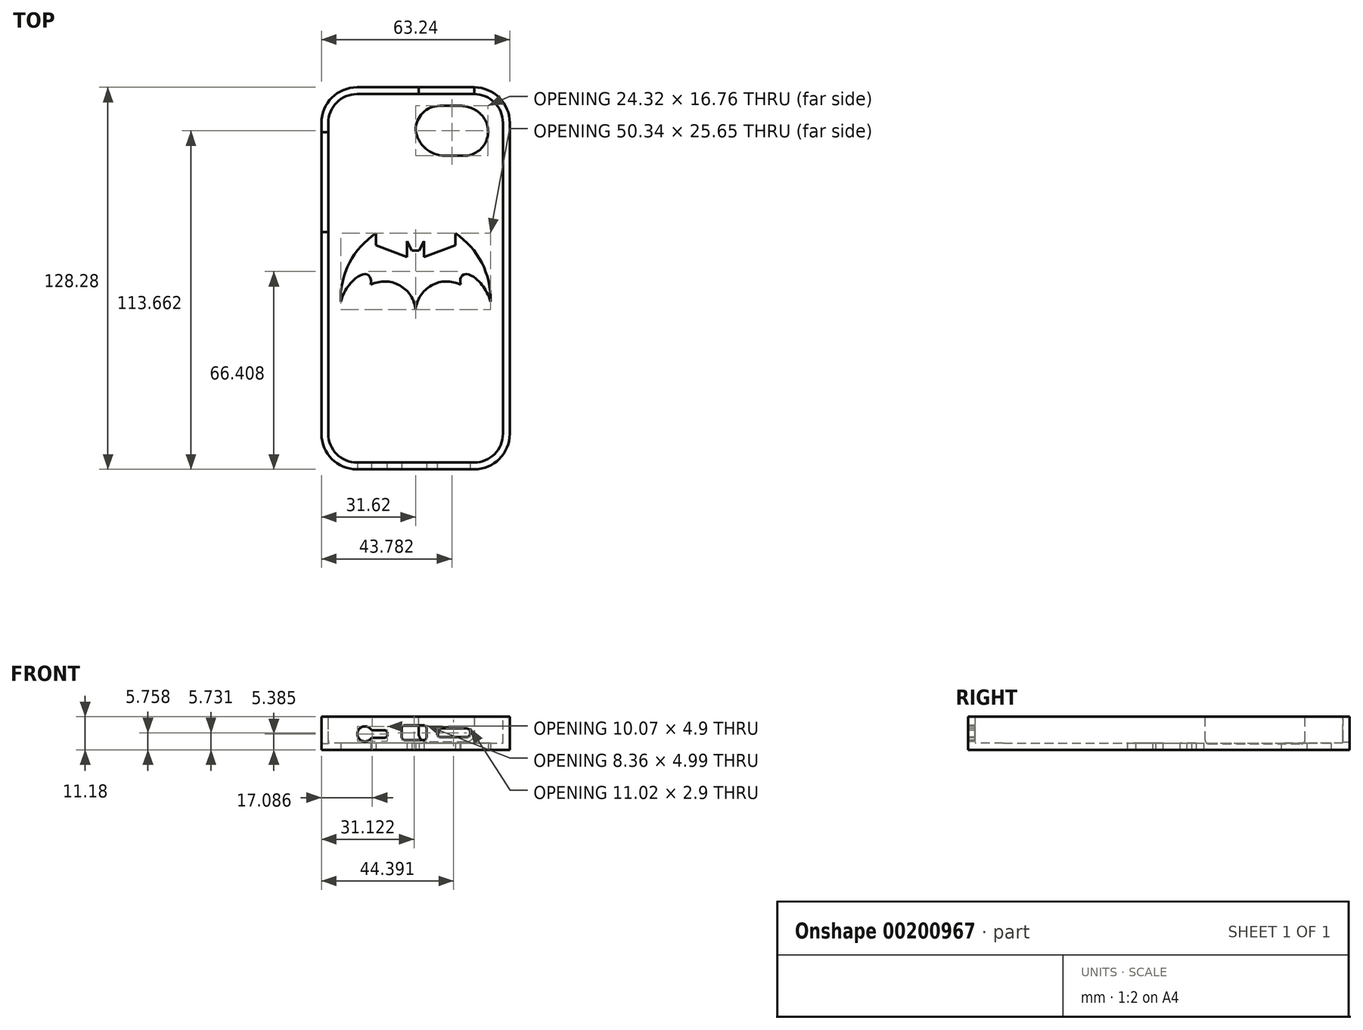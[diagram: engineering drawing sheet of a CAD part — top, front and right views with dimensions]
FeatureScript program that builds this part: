
annotation { "Feature Type Name" : "Feature", "Feature Type Description" : "" }
export const myFeature = defineFeature(function(context is Context, id is Id, definition is map)
    precondition{}
    {
        {
            var Q0;
            Q0=qCreatedBy(makeId("Top.planeOp"),FACE);
            var sketch = newSketch(context, id + "F0", { "sketchPlane" : qUnion([Q0])});
            skLineSegment(sketch, "E0.bottom", {"start": v(31.62, -64.13) * mm, "end": v(-31.62, -64.13) * mm});
            skLineSegment(sketch, "E0.top", {"start": v(31.62, 64.13) * mm, "end": v(-31.62, 64.13) * mm});
            skLineSegment(sketch, "E0.left", {"start": v(31.62, -64.13) * mm, "end": v(31.62, 64.14) * mm});
            skLineSegment(sketch, "E0.right", {"start": v(-31.62, -64.13) * mm, "end": v(-31.62, 64.14) * mm});
            skPoint(sketch, "E0.middle", {"position": v(0, 0) * mm});
            skSolve(sketch);
        }
        {
            var Q0;
            Q0=makeQuery(id+"F0.imprint","IMPRINT",FACE,{"disambiguationData":[TD([[makeQuery(id+"F0.imprint","IMPRINT",EDGE,{"derivedFrom":sQuery(id+"F0.wireOp",EDGE,"E0.bottom")}),-1.0]])]});
            extrude(context, id + "F1", {"entities" : qUnion([Q0]), "depth" : 11.18 * mm});
        }
        {
            var Q0;
            Q0=makeQuery(id+"F1.opExtrude","SWEPT_EDGE",EDGE,{"disambiguationData":[OSD([sQuery(id+"F0.wireOp",EDGE,"E0.bottom"),sQuery(id+"F0.wireOp",EDGE,"E0.right")])]});
            fillet(context, id + "F2", {"entities" : qUnion([Q0]), "radius" : 11.94 * mm, "tangentPropagation" : true, "allowEdgeOverflow" : false});
        }
        {
            var Q0;
            Q0=makeQuery(id+"F1.opExtrude","SWEPT_EDGE",EDGE,{"disambiguationData":[OSD([sQuery(id+"F0.wireOp",EDGE,"E0.bottom"),sQuery(id+"F0.wireOp",EDGE,"E0.left")])]});
            fillet(context, id + "F3", {"entities" : qUnion([Q0]), "radius" : 11.94 * mm, "tangentPropagation" : true, "allowEdgeOverflow" : false});
        }
        {
            var Q0;
            Q0=makeQuery(id+"F1.opExtrude","SWEPT_EDGE",EDGE,{"disambiguationData":[OSD([sQuery(id+"F0.wireOp",EDGE,"E0.top"),sQuery(id+"F0.wireOp",EDGE,"E0.right")])]});
            fillet(context, id + "F4", {"entities" : qUnion([Q0]), "radius" : 11.94 * mm, "tangentPropagation" : true, "allowEdgeOverflow" : false});
        }
        {
            var Q0;
            Q0=makeQuery(id+"F1.opExtrude","SWEPT_EDGE",EDGE,{"disambiguationData":[OSD([sQuery(id+"F0.wireOp",EDGE,"E0.top"),sQuery(id+"F0.wireOp",EDGE,"E0.left")])]});
            fillet(context, id + "F5", {"entities" : qUnion([Q0]), "radius" : 11.94 * mm, "tangentPropagation" : true, "allowEdgeOverflow" : false});
        }
        {
            var Q0;
            Q0=makeQuery(id+"F1.opExtrude","CAP_FACE",FACE,{"disambiguationData":[OSD([sQuery(id+"F0.wireOp",EDGE,"E0.bottom"),sQuery(id+"F0.wireOp",EDGE,"E0.top"),sQuery(id+"F0.wireOp",EDGE,"E0.left"),sQuery(id+"F0.wireOp",EDGE,"E0.right")])],"isStart":false});
            shell(context, id + "F6", {"entities" : qUnion([Q0]), "thickness" : 2.3 * mm});
        }
        {
            var Q0;
            Q0=makeQuery(id+"F1.opExtrude","CAP_FACE",FACE,{"disambiguationData":[OSD([sQuery(id+"F0.wireOp",EDGE,"E0.bottom"),sQuery(id+"F0.wireOp",EDGE,"E0.top"),sQuery(id+"F0.wireOp",EDGE,"E0.left"),sQuery(id+"F0.wireOp",EDGE,"E0.right")])],"isStart":true});
            var sketch = newSketch(context, id + "F7", { "sketchPlane" : qUnion([Q0])});
            skLineSegment(sketch, "E1", {"start": v(24.9, -57.9) * mm, "end": v(0, -57.9) * mm});
            skLineSegment(sketch, "E2", {"start": v(0, -57.9) * mm, "end": v(0, -41.14) * mm});
            skLineSegment(sketch, "E3", {"start": v(24.9, -57.9) * mm, "end": v(24.9, -41.14) * mm});
            skLineSegment(sketch, "E4", {"start": v(24.9, -41.14) * mm, "end": v(0, -41.14) * mm});
            skSolve(sketch);
        }
        {
            var Q0;
            Q0=makeQuery(id+"F7.imprint","IMPRINT",FACE,{"disambiguationData":[TD([[makeQuery(id+"F7.imprint","IMPRINT",EDGE,{"derivedFrom":sQuery(id+"F7.wireOp",EDGE,"E1")}),-1.0]])]});
            extrude(context, id + "F8", {"entities" : qUnion([Q0]), "operationType" : NewBodyOperationType.REMOVE, "oppositeDirection" : true, "depth" : 25.4 * mm});
        }
        {
            var Q0;
            Q0=makeQuery(id+"F8.boolean.opBoolean","COPY",EDGE,{"derivedFrom":makeQuery(id+"F8.opExtrude","SWEPT_EDGE",EDGE,{"disambiguationData":[OSD([sQuery(id+"F7.wireOp",EDGE,"E1"),sQuery(id+"F7.wireOp",EDGE,"E2")])]})});
            fillet(context, id + "F9", {"entities" : qUnion([Q0]), "radius" : 8.13 * mm, "tangentPropagation" : true, "allowEdgeOverflow" : false});
        }
        {
            var Q0;
            Q0=makeQuery(id+"F8.boolean.opBoolean","COPY",EDGE,{"derivedFrom":makeQuery(id+"F8.opExtrude","SWEPT_EDGE",EDGE,{"disambiguationData":[OSD([sQuery(id+"F7.wireOp",EDGE,"E1"),sQuery(id+"F7.wireOp",EDGE,"E3")])]})});
            fillet(context, id + "F10", {"entities" : qUnion([Q0]), "radius" : 9.9 * mm, "tangentPropagation" : true, "allowEdgeOverflow" : false});
        }
        {
            var Q0;
            Q0=makeQuery(id+"F8.boolean.opBoolean","COPY",EDGE,{"derivedFrom":makeQuery(id+"F8.opExtrude","SWEPT_EDGE",EDGE,{"disambiguationData":[OSD([sQuery(id+"F7.wireOp",EDGE,"E3"),sQuery(id+"F7.wireOp",EDGE,"E4")])]})});
            fillet(context, id + "F11", {"entities" : qUnion([Q0]), "radius" : 8.13 * mm, "tangentPropagation" : true, "allowEdgeOverflow" : false});
        }
        {
            var Q0;
            Q0=makeQuery(id+"F8.boolean.opBoolean","COPY",EDGE,{"derivedFrom":makeQuery(id+"F8.opExtrude","SWEPT_EDGE",EDGE,{"disambiguationData":[OSD([sQuery(id+"F7.wireOp",EDGE,"E2"),sQuery(id+"F7.wireOp",EDGE,"E4")])]})});
            fillet(context, id + "F12", {"entities" : qUnion([Q0]), "radius" : 9.9 * mm, "tangentPropagation" : true, "allowEdgeOverflow" : false});
        }
        {
            var Q0;
            Q0=makeQuery(id+"F1.opExtrude","CAP_FACE",FACE,{"disambiguationData":[OSD([sQuery(id+"F0.wireOp",EDGE,"E0.bottom"),sQuery(id+"F0.wireOp",EDGE,"E0.top"),sQuery(id+"F0.wireOp",EDGE,"E0.left"),sQuery(id+"F0.wireOp",EDGE,"E0.right")])],"isStart":false});
            var sketch = newSketch(context, id + "F13", { "sketchPlane" : qUnion([Q0])});
            skLineSegment(sketch, "E5.bottom", {"start": v(-29.34, 49.08) * mm, "end": v(-31.62, 49.08) * mm});
            skLineSegment(sketch, "E5.top", {"start": v(-29.34, 15.55) * mm, "end": v(-31.62, 15.55) * mm});
            skLineSegment(sketch, "E5.left", {"start": v(-29.34, 49.08) * mm, "end": v(-29.34, 15.55) * mm});
            skLineSegment(sketch, "E5.right", {"start": v(-31.62, 49.08) * mm, "end": v(-31.62, 15.55) * mm});
            skSolve(sketch);
        }
        {
            var Q0;
            Q0=makeQuery(id+"F13.imprint","IMPRINT",FACE,{"disambiguationData":[TD([[makeQuery(id+"F13.imprint","IMPRINT",EDGE,{"derivedFrom":sQuery(id+"F13.wireOp",EDGE,"E5.bottom")}),1.0]])]});
            extrude(context, id + "F14", {"entities" : qUnion([Q0]), "operationType" : NewBodyOperationType.REMOVE, "oppositeDirection" : true, "depth" : 9.14 * mm});
        }
        {
            var Q0;
            Q0=makeQuery(id+"F14.boolean.opBoolean","COPY",EDGE,{"derivedFrom":makeQuery(id+"F14.opExtrude","CAP_EDGE",EDGE,{"disambiguationData":[OSD([sQuery(id+"F13.wireOp",EDGE,"E5.bottom")])],"isStart":false})});
            fillet(context, id + "F15", {"entities" : qUnion([Q0]), "radius" : 1.23 * mm, "tangentPropagation" : true, "allowEdgeOverflow" : false});
        }
        {
            var Q0;
            Q0=makeQuery(id+"F14.boolean.opBoolean","COPY",EDGE,{"derivedFrom":makeQuery(id+"F14.opExtrude","CAP_EDGE",EDGE,{"disambiguationData":[OSD([sQuery(id+"F13.wireOp",EDGE,"E5.top")])],"isStart":false})});
            fillet(context, id + "F16", {"entities" : qUnion([Q0]), "radius" : 1.22 * mm, "tangentPropagation" : true, "allowEdgeOverflow" : false});
        }
        {
            var Q0;
            Q0=makeQuery(id+"F1.opExtrude","SWEPT_FACE",FACE,{"disambiguationData":[OSD([sQuery(id+"F0.wireOp",EDGE,"E0.bottom")])]});
            var sketch = newSketch(context, id + "F17", { "sketchPlane" : qUnion([Q0])});
            skArc(sketch, "E6", {"start": v(-14.81, 6.6) * mm, "mid": v(-19.57, 5.42) * mm, "end": v(-14.87, 4.04) * mm});
            skLineSegment(sketch, "E7", {"start": v(-14.81, 6.6) * mm, "end": v(-9.48, 6.6) * mm});
            skLineSegment(sketch, "E8", {"start": v(-14.87, 4.04) * mm, "end": v(-9.53, 4.04) * mm});
            skLineSegment(sketch, "E9", {"start": v(-9.48, 6.6) * mm, "end": v(-9.53, 4.04) * mm});
            skSolve(sketch);
        }
        {
            var Q0;
            Q0=makeQuery(id+"F17.imprint","IMPRINT",FACE,{"disambiguationData":[TD([[makeQuery(id+"F17.imprint","IMPRINT",EDGE,{"derivedFrom":sQuery(id+"F17.wireOp",EDGE,"E6")}),1.0]])]});
            extrude(context, id + "F18", {"entities" : qUnion([Q0]), "operationType" : NewBodyOperationType.REMOVE, "oppositeDirection" : true, "depth" : 25.4 * mm});
        }
        {
            var Q0;
            Q0=makeQuery(id+"F18.boolean.opBoolean","COPY",EDGE,{"derivedFrom":makeQuery(id+"F18.opExtrude","SWEPT_EDGE",EDGE,{"disambiguationData":[OSD([sQuery(id+"F17.wireOp",EDGE,"E7"),sQuery(id+"F17.wireOp",EDGE,"E9")])]})});
            fillet(context, id + "F19", {"entities" : qUnion([Q0]), "radius" : 1.02 * mm, "tangentPropagation" : true, "allowEdgeOverflow" : false});
        }
        {
            var Q0;
            Q0=makeQuery(id+"F18.boolean.opBoolean","COPY",EDGE,{"derivedFrom":makeQuery(id+"F18.opExtrude","SWEPT_EDGE",EDGE,{"disambiguationData":[OSD([sQuery(id+"F17.wireOp",EDGE,"E8"),sQuery(id+"F17.wireOp",EDGE,"E9")])]})});
            fillet(context, id + "F20", {"entities" : qUnion([Q0]), "radius" : 1.02 * mm, "tangentPropagation" : true, "allowEdgeOverflow" : false});
        }
        {
            var Q0;
            Q0=makeQuery(id+"F1.opExtrude","SWEPT_FACE",FACE,{"disambiguationData":[OSD([sQuery(id+"F0.wireOp",EDGE,"E0.bottom")])]});
            var sketch = newSketch(context, id + "F21", { "sketchPlane" : qUnion([Q0])});
            skLineSegment(sketch, "E10.bottom", {"start": v(3.68, 3.27) * mm, "end": v(-4.68, 3.27) * mm});
            skLineSegment(sketch, "E10.top", {"start": v(3.68, 8.25) * mm, "end": v(-4.68, 8.25) * mm});
            skLineSegment(sketch, "E10.left", {"start": v(3.68, 3.27) * mm, "end": v(3.68, 8.25) * mm});
            skLineSegment(sketch, "E10.right", {"start": v(-4.68, 3.27) * mm, "end": v(-4.68, 8.25) * mm});
            skSolve(sketch);
        }
        {
            var Q0;
            Q0=makeQuery(id+"F21.imprint","IMPRINT",FACE,{"disambiguationData":[TD([[makeQuery(id+"F21.imprint","IMPRINT",EDGE,{"derivedFrom":sQuery(id+"F21.wireOp",EDGE,"E10.bottom")}),-1.0]])]});
            extrude(context, id + "F22", {"entities" : qUnion([Q0]), "operationType" : NewBodyOperationType.REMOVE, "oppositeDirection" : true, "depth" : 25.4 * mm});
        }
        {
            var Q0;
            Q0=makeQuery(id+"F22.boolean.opBoolean","COPY",EDGE,{"derivedFrom":makeQuery(id+"F22.opExtrude","SWEPT_EDGE",EDGE,{"disambiguationData":[OSD([sQuery(id+"F21.wireOp",EDGE,"E10.bottom"),sQuery(id+"F21.wireOp",EDGE,"E10.right")])]})});
            fillet(context, id + "F23", {"entities" : qUnion([Q0]), "radius" : 1.1 * mm, "tangentPropagation" : true, "allowEdgeOverflow" : false});
        }
        {
            var Q0;
            Q0=makeQuery(id+"F22.boolean.opBoolean","COPY",EDGE,{"derivedFrom":makeQuery(id+"F22.opExtrude","SWEPT_EDGE",EDGE,{"disambiguationData":[OSD([sQuery(id+"F21.wireOp",EDGE,"E10.bottom"),sQuery(id+"F21.wireOp",EDGE,"E10.left")])]})});
            fillet(context, id + "F24", {"entities" : qUnion([Q0]), "radius" : 1.1 * mm, "tangentPropagation" : true, "allowEdgeOverflow" : false});
        }
        {
            var Q0;
            Q0=makeQuery(id+"F22.boolean.opBoolean","COPY",EDGE,{"derivedFrom":makeQuery(id+"F22.opExtrude","SWEPT_EDGE",EDGE,{"disambiguationData":[OSD([sQuery(id+"F21.wireOp",EDGE,"E10.top"),sQuery(id+"F21.wireOp",EDGE,"E10.right")])]})});
            fillet(context, id + "F25", {"entities" : qUnion([Q0]), "radius" : 1.1 * mm, "tangentPropagation" : true, "allowEdgeOverflow" : false});
        }
        {
            var Q0;
            Q0=makeQuery(id+"F22.boolean.opBoolean","COPY",EDGE,{"derivedFrom":makeQuery(id+"F22.opExtrude","SWEPT_EDGE",EDGE,{"disambiguationData":[OSD([sQuery(id+"F21.wireOp",EDGE,"E10.top"),sQuery(id+"F21.wireOp",EDGE,"E10.left")])]})});
            fillet(context, id + "F26", {"entities" : qUnion([Q0]), "radius" : 1.1 * mm, "tangentPropagation" : true, "allowEdgeOverflow" : false});
        }
        {
            var Q0;
            Q0=makeQuery(id+"F1.opExtrude","SWEPT_FACE",FACE,{"disambiguationData":[OSD([sQuery(id+"F0.wireOp",EDGE,"E0.bottom")])]});
            var sketch = newSketch(context, id + "F27", { "sketchPlane" : qUnion([Q0])});
            skLineSegment(sketch, "E11.bottom", {"start": v(7.26, 7.18) * mm, "end": v(18.28, 7.18) * mm});
            skLineSegment(sketch, "E11.top", {"start": v(7.26, 4.28) * mm, "end": v(18.28, 4.28) * mm});
            skLineSegment(sketch, "E11.left", {"start": v(7.26, 7.18) * mm, "end": v(7.26, 4.28) * mm});
            skLineSegment(sketch, "E11.right", {"start": v(18.28, 7.18) * mm, "end": v(18.28, 4.28) * mm});
            skSolve(sketch);
        }
        {
            var Q0;
            Q0=makeQuery(id+"F27.imprint","IMPRINT",FACE,{"disambiguationData":[TD([[makeQuery(id+"F27.imprint","IMPRINT",EDGE,{"derivedFrom":sQuery(id+"F27.wireOp",EDGE,"E11.bottom")}),-1.0]])]});
            extrude(context, id + "F28", {"entities" : qUnion([Q0]), "operationType" : NewBodyOperationType.REMOVE, "oppositeDirection" : true, "depth" : 23.72 * mm});
        }
        {
            var Q0;
            Q0=makeQuery(id+"F28.boolean.opBoolean","COPY",EDGE,{"derivedFrom":makeQuery(id+"F28.opExtrude","SWEPT_EDGE",EDGE,{"disambiguationData":[OSD([sQuery(id+"F27.wireOp",EDGE,"E11.bottom"),sQuery(id+"F27.wireOp",EDGE,"E11.left")])]})});
            fillet(context, id + "F29", {"entities" : qUnion([Q0]), "radius" : 1.1 * mm, "tangentPropagation" : true, "allowEdgeOverflow" : false});
        }
        {
            var Q0;
            Q0=makeQuery(id+"F28.boolean.opBoolean","COPY",EDGE,{"derivedFrom":makeQuery(id+"F28.opExtrude","SWEPT_EDGE",EDGE,{"disambiguationData":[OSD([sQuery(id+"F27.wireOp",EDGE,"E11.top"),sQuery(id+"F27.wireOp",EDGE,"E11.left")])]})});
            fillet(context, id + "F30", {"entities" : qUnion([Q0]), "radius" : 1.1 * mm, "tangentPropagation" : true, "allowEdgeOverflow" : false});
        }
        {
            var Q0;
            Q0=makeQuery(id+"F28.boolean.opBoolean","COPY",EDGE,{"derivedFrom":makeQuery(id+"F28.opExtrude","SWEPT_EDGE",EDGE,{"disambiguationData":[OSD([sQuery(id+"F27.wireOp",EDGE,"E11.bottom"),sQuery(id+"F27.wireOp",EDGE,"E11.right")])]})});
            fillet(context, id + "F31", {"entities" : qUnion([Q0]), "radius" : 1.1 * mm, "tangentPropagation" : true, "allowEdgeOverflow" : false});
        }
        {
            var Q0;
            Q0=makeQuery(id+"F28.boolean.opBoolean","COPY",EDGE,{"derivedFrom":makeQuery(id+"F28.opExtrude","SWEPT_EDGE",EDGE,{"disambiguationData":[OSD([sQuery(id+"F27.wireOp",EDGE,"E11.top"),sQuery(id+"F27.wireOp",EDGE,"E11.right")])]})});
            fillet(context, id + "F32", {"entities" : qUnion([Q0]), "radius" : 1.1 * mm, "tangentPropagation" : true, "allowEdgeOverflow" : false});
        }
        {
            var Q0;
            Q0=makeQuery(id+"F1.opExtrude","CAP_FACE",FACE,{"disambiguationData":[OSD([sQuery(id+"F0.wireOp",EDGE,"E0.bottom"),sQuery(id+"F0.wireOp",EDGE,"E0.top"),sQuery(id+"F0.wireOp",EDGE,"E0.left"),sQuery(id+"F0.wireOp",EDGE,"E0.right")])],"isStart":true});
            var sketch = newSketch(context, id + "F33", { "sketchPlane" : qUnion([Q0])});
            skArc(sketch, "E12", {"start": v(0, 12.55) * mm, "mid": v(4.49, 2.92) * mm, "end": v(15.09, 2.14) * mm});
            skFitSpline(sketch, "E13", {"points": [v(15.09, 2.14) * mm, v(15.09, 0) * mm, v(16.72, -1.43) * mm, v(20.13, 0) * mm, v(22.24, 2.14) * mm, v(23.87, 4.58) * mm, v(25.17, 7.84) * mm], "startDerivative": vector(-2.46, -15.22) * mm, "endDerivative": vector(6.42, 18.44) * mm});
            skArc(sketch, "E14", {"start": v(13.3, -15.1) * mm, "mid": v(22.23, -5.18) * mm, "end": v(25.17, 7.84) * mm});
            skLineSegment(sketch, "E15", {"start": v(13.3, -15.1) * mm, "end": v(13.3, -11.03) * mm});
            skLineSegment(sketch, "E16", {"start": v(13.3, -11.03) * mm, "end": v(2.87, -7.11) * mm});
            skLineSegment(sketch, "E17", {"start": v(2.87, -7.11) * mm, "end": v(2.87, -12.5) * mm});
            skLineSegment(sketch, "E18", {"start": v(2.87, -12.5) * mm, "end": v(1.19, -9.28) * mm});
            skLineSegment(sketch, "E19", {"start": v(1.19, -9.28) * mm, "end": v(0, -9.28) * mm});
            skLineSegment(sketch, "E20", {"start": v(0, -9.28) * mm, "end": v(0, 12.55) * mm});
            skArc(sketch, "E21.MirrorCS", {"start": v(0, 12.55) * mm, "mid": v(-4.49, 2.92) * mm, "end": v(-15.09, 2.14) * mm});
            skLineSegment(sketch, "E22.MirrorCS", {"start": v(-13.3, -11.03) * mm, "end": v(-2.87, -7.11) * mm});
            skLineSegment(sketch, "E23.MirrorCS", {"start": v(-13.3, -15.1) * mm, "end": v(-13.3, -11.03) * mm});
            skArc(sketch, "E24.MirrorCS", {"start": v(-13.3, -15.1) * mm, "mid": v(-22.23, -5.18) * mm, "end": v(-25.17, 7.84) * mm});
            skFitSpline(sketch, "E25.MirrorCS", {"points": [v(-15.09, 2.14) * mm, v(-15.09, 0) * mm, v(-16.72, -1.43) * mm, v(-20.13, 0) * mm, v(-22.24, 2.14) * mm, v(-23.87, 4.58) * mm, v(-25.17, 7.84) * mm], "startDerivative": vector(2.46, -15.22) * mm, "endDerivative": vector(-6.42, 18.44) * mm});
            skLineSegment(sketch, "E26.MirrorCS", {"start": v(-2.87, -7.11) * mm, "end": v(-2.87, -12.5) * mm});
            skLineSegment(sketch, "E27.MirrorCS", {"start": v(-2.87, -12.5) * mm, "end": v(-1.19, -9.28) * mm});
            skLineSegment(sketch, "E28.MirrorCS", {"start": v(-1.19, -9.28) * mm, "end": v(0, -9.28) * mm});
            skSolve(sketch);
        }
        {
            var Q0;
            {var subQ0=sQuery(id+"F33.wireOp",EDGE,"E13");Q0=makeQuery(id+"F33.imprint","IMPRINT",FACE,{"disambiguationData":[TD([[makeQuery(id+"F33.imprint","IMPRINT",EDGE,{"derivedFrom":subQ0}),-1.0]])]});}
            var Q1;
            Q1=makeQuery(id+"F33.imprint","IMPRINT",FACE,{"disambiguationData":[TD([[makeQuery(id+"F33.imprint","IMPRINT",EDGE,{"derivedFrom":sQuery(id+"F33.wireOp",EDGE,"E22.MirrorCS")}),1.0]])]});
            extrude(context, id + "F34", {"entities" : qUnion([Q0, Q1]), "operationType" : NewBodyOperationType.REMOVE, "oppositeDirection" : true, "depth" : 33.02 * mm});
        }
        {
            var Q0;
            Q0=makeQuery(id+"F1.opExtrude","CAP_FACE",FACE,{"disambiguationData":[OSD([sQuery(id+"F0.wireOp",EDGE,"E0.bottom"),sQuery(id+"F0.wireOp",EDGE,"E0.top"),sQuery(id+"F0.wireOp",EDGE,"E0.left"),sQuery(id+"F0.wireOp",EDGE,"E0.right")])],"isStart":false});
            var sketch = newSketch(context, id + "F35", { "sketchPlane" : qUnion([Q0])});
            skLineSegment(sketch, "E29.bottom", {"start": v(19.69, 61.85) * mm, "end": v(1.01, 61.85) * mm});
            skLineSegment(sketch, "E29.top", {"start": v(19.69, 64.13) * mm, "end": v(1.01, 64.13) * mm});
            skLineSegment(sketch, "E29.left", {"start": v(19.69, 61.85) * mm, "end": v(19.69, 64.13) * mm});
            skLineSegment(sketch, "E29.right", {"start": v(1.01, 61.85) * mm, "end": v(1.01, 64.13) * mm});
            skSolve(sketch);
        }
        {
            var Q0;
            Q0=makeQuery(id+"F35.imprint","IMPRINT",FACE,{"disambiguationData":[TD([[makeQuery(id+"F35.imprint","IMPRINT",EDGE,{"derivedFrom":sQuery(id+"F35.wireOp",EDGE,"E29.bottom")}),-1.0]])]});
            extrude(context, id + "F36", {"entities" : qUnion([Q0]), "operationType" : NewBodyOperationType.REMOVE, "oppositeDirection" : true, "depth" : 8.53 * mm});
        }
        {
            var Q0;
            Q0=makeQuery(id+"F36.boolean.opBoolean","COPY",EDGE,{"derivedFrom":makeQuery(id+"F36.opExtrude","CAP_EDGE",EDGE,{"disambiguationData":[OSD([sQuery(id+"F35.wireOp",EDGE,"E29.left")])],"isStart":false})});
            var Q1;
            Q1=makeQuery(id+"F36.boolean.opBoolean","COPY",EDGE,{"derivedFrom":makeQuery(id+"F36.opExtrude","CAP_EDGE",EDGE,{"disambiguationData":[OSD([sQuery(id+"F35.wireOp",EDGE,"E29.right")])],"isStart":false})});
            fillet(context, id + "F37", {"entities" : qUnion([Q0, Q1]), "radius" : 2.88 * mm, "tangentPropagation" : true, "allowEdgeOverflow" : false});
        }
    });
